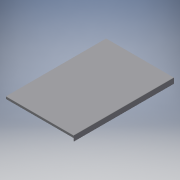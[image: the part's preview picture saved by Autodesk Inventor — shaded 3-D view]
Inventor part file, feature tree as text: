
AUTODESK INVENTOR PART (.ipt)
format: ipt  version: 2016 (Build 200138000, 138)  size: 268,288 bytes
history: native  units: in
note: dims shown in document units (in); Inventor stores cm internally (conversion verified against a paired STEP export)
features: sketch x7, other x3
ambient origin geometry x8: Origin, YZ Plane, XZ Plane, XY Plane, X Axis, Y Axis, Z Axis, Center Point
bodies: Solid1 (feature_tree)
feature tree (10):
  other  "SheedSide.ipt"
  other  "Solid1::SheedSide.ipt"
  other  "TaggingFeature1"
  sketch  "Sketch1"  dims[d0=0.3937in]
  sketch  "Sketch2"
  sketch  "Sketch3"
  sketch  "Sketch4"
  sketch  "Sketch5"
  sketch  "Sketch6"
  sketch  "Sketch7"
